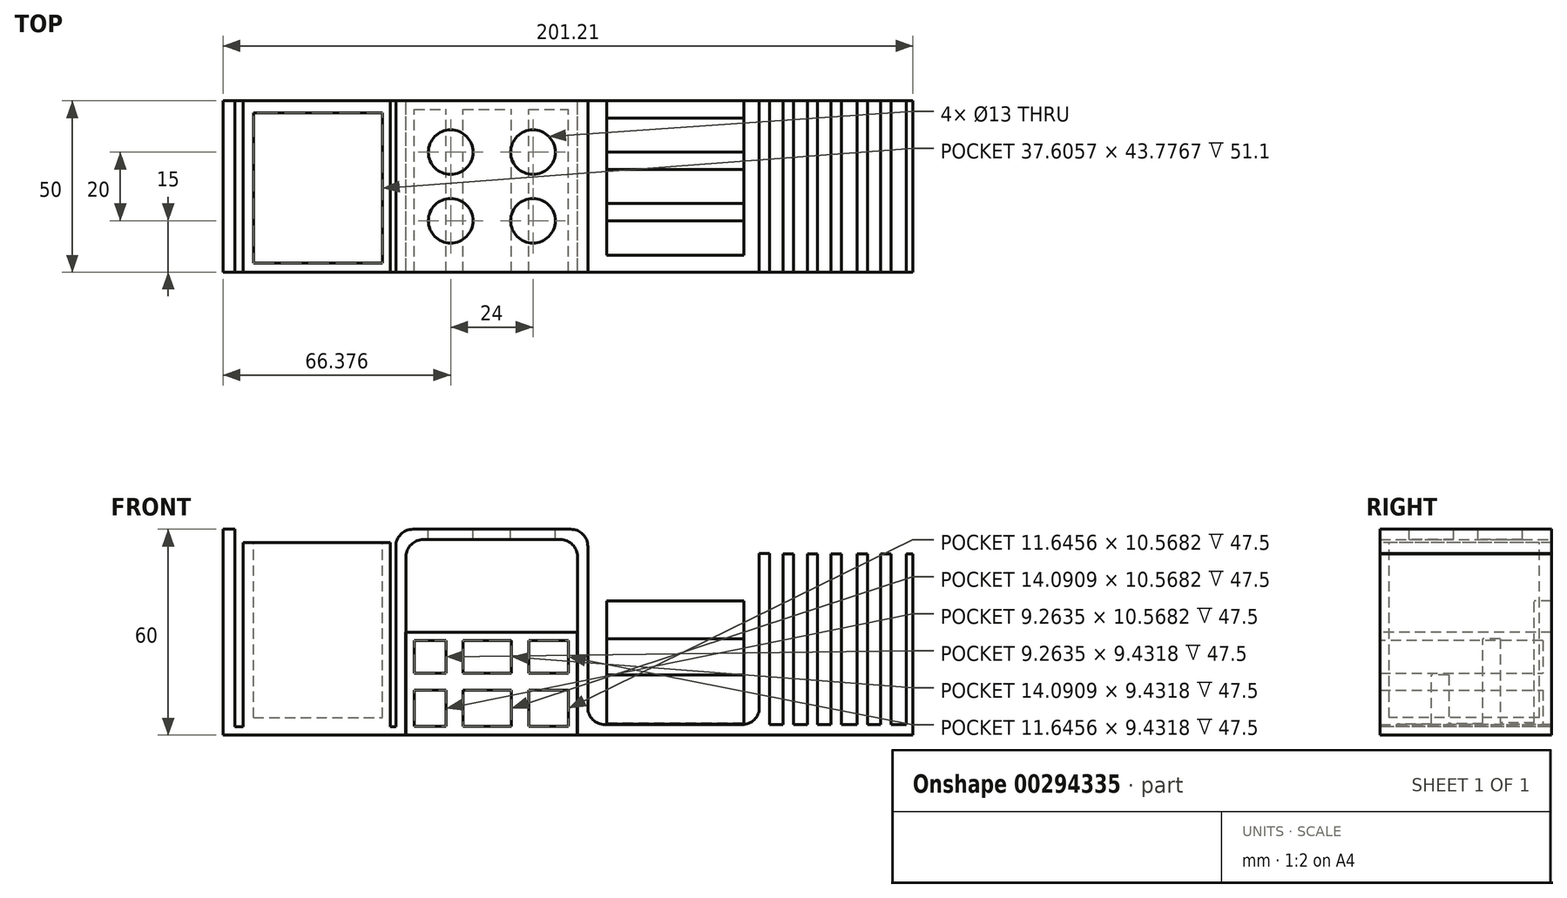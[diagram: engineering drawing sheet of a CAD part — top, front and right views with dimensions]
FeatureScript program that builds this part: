
annotation { "Feature Type Name" : "Feature", "Feature Type Description" : "" }
export const myFeature = defineFeature(function(context is Context, id is Id, definition is map)
    precondition{}
    {
        {
            var Q0;
            Q0=qCreatedBy(makeId("Front.planeOp"),FACE);
            var sketch = newSketch(context, id + "F0", { "sketchPlane" : qUnion([Q0])});
            skLineSegment(sketch, "E0.top", {"start": v(4.58, 57) * mm, "end": v(54.58, 57) * mm});
            skLineSegment(sketch, "E0.left", {"start": v(4.58, 0) * mm, "end": v(4.58, 57) * mm});
            skLineSegment(sketch, "E0.right", {"start": v(54.58, 0) * mm, "end": v(54.58, 57) * mm});
            skLineSegment(sketch, "E1.top", {"start": v(57.58, 3) * mm, "end": v(107.58, 3) * mm});
            skLineSegment(sketch, "E1.left", {"start": v(57.58, 60) * mm, "end": v(57.58, 3) * mm});
            skLineSegment(sketch, "E1.right", {"start": v(107.58, 53) * mm, "end": v(107.58, 3) * mm});
            skLineSegment(sketch, "E2", {"start": v(1.58, 0) * mm, "end": v(4.58, 0) * mm});
            skLineSegment(sketch, "E3", {"start": v(54.58, 0) * mm, "end": v(110.58, 0) * mm});
            skLineSegment(sketch, "E4", {"start": v(1.58, 60) * mm, "end": v(57.58, 60) * mm});
            skLineSegment(sketch, "E5", {"start": v(110.58, 53) * mm, "end": v(107.58, 53) * mm});
            skLineSegment(sketch, "E6.bottom", {"start": v(1.58, 0) * mm, "end": v(-45.36, 0) * mm});
            skLineSegment(sketch, "E6.top", {"start": v(1.58, 2.45) * mm, "end": v(-45.36, 2.45) * mm});
            skLineSegment(sketch, "E7.bottom", {"start": v(-45.36, 0) * mm, "end": v(-48.8, 0) * mm});
            skLineSegment(sketch, "E7.top", {"start": v(-45.36, 60) * mm, "end": v(-48.8, 60) * mm});
            skLineSegment(sketch, "E7.right", {"start": v(-48.8, 0) * mm, "end": v(-48.8, 60) * mm});
            skLineSegment(sketch, "E8", {"start": v(-45.36, 60) * mm, "end": v(-45.36, 2.45) * mm});
            skLineSegment(sketch, "E9", {"start": v(1.58, 60) * mm, "end": v(1.58, 2.45) * mm});
            skLineSegment(sketch, "E10.bottom", {"start": v(110.58, 0) * mm, "end": v(152.41, 0) * mm});
            skLineSegment(sketch, "E10.top", {"start": v(110.58, 3.01) * mm, "end": v(152.41, 3.01) * mm});
            skLineSegment(sketch, "E10.right", {"start": v(152.41, 0) * mm, "end": v(152.41, 3.01) * mm});
            skLineSegment(sketch, "E11", {"start": v(110.58, 53) * mm, "end": v(110.58, 3.01) * mm});
            skLineSegment(sketch, "E12.bottom", {"start": v(114.5, 3.01) * mm, "end": v(117.5, 3.01) * mm});
            skLineSegment(sketch, "E12.top", {"start": v(114.5, 52.83) * mm, "end": v(117.5, 52.83) * mm});
            skLineSegment(sketch, "E12.left", {"start": v(114.5, 3.01) * mm, "end": v(114.5, 52.83) * mm});
            skLineSegment(sketch, "E12.right", {"start": v(117.5, 3.01) * mm, "end": v(117.5, 52.83) * mm});
            skLineSegment(sketch, "E13.bottom", {"start": v(121.6, 3.01) * mm, "end": v(124.6, 3.01) * mm});
            skLineSegment(sketch, "E13.top", {"start": v(121.6, 52.83) * mm, "end": v(124.6, 52.83) * mm});
            skLineSegment(sketch, "E13.left", {"start": v(121.6, 3.01) * mm, "end": v(121.6, 52.83) * mm});
            skLineSegment(sketch, "E13.right", {"start": v(124.6, 3.01) * mm, "end": v(124.6, 52.83) * mm});
            skLineSegment(sketch, "E14.bottom", {"start": v(128.48, 3.01) * mm, "end": v(131.48, 3.01) * mm});
            skLineSegment(sketch, "E14.top", {"start": v(128.48, 52.83) * mm, "end": v(131.48, 52.83) * mm});
            skLineSegment(sketch, "E14.left", {"start": v(128.48, 3.01) * mm, "end": v(128.48, 52.83) * mm});
            skLineSegment(sketch, "E14.right", {"start": v(131.48, 3.01) * mm, "end": v(131.48, 52.83) * mm});
            skLineSegment(sketch, "E15.bottom", {"start": v(136.1, 3.01) * mm, "end": v(139.1, 3.01) * mm});
            skLineSegment(sketch, "E15.top", {"start": v(136.1, 52.83) * mm, "end": v(139.1, 52.83) * mm});
            skLineSegment(sketch, "E15.left", {"start": v(136.1, 3.01) * mm, "end": v(136.1, 52.83) * mm});
            skLineSegment(sketch, "E15.right", {"start": v(139.1, 3.01) * mm, "end": v(139.1, 52.83) * mm});
            skLineSegment(sketch, "E16.bottom", {"start": v(142.98, 3.01) * mm, "end": v(145.98, 3.01) * mm});
            skLineSegment(sketch, "E16.top", {"start": v(142.98, 52.83) * mm, "end": v(145.98, 52.83) * mm});
            skLineSegment(sketch, "E16.left", {"start": v(142.98, 3.01) * mm, "end": v(142.98, 52.83) * mm});
            skLineSegment(sketch, "E16.right", {"start": v(145.98, 3.01) * mm, "end": v(145.98, 52.83) * mm});
            skLineSegment(sketch, "E17.bottom", {"start": v(152.41, 3.01) * mm, "end": v(150.41, 3.01) * mm});
            skLineSegment(sketch, "E17.top", {"start": v(152.41, 52.83) * mm, "end": v(150.41, 52.83) * mm});
            skLineSegment(sketch, "E17.left", {"start": v(152.41, 3.01) * mm, "end": v(152.41, 52.83) * mm});
            skLineSegment(sketch, "E17.right", {"start": v(150.41, 3.01) * mm, "end": v(150.41, 52.83) * mm});
            skLineSegment(sketch, "E18", {"start": v(107.58, 3) * mm, "end": v(107.58, 0) * mm});
            skSolve(sketch);
        }
        {
            var Q0;
            Q0 = qSketchRegion(id + "F0", true);
            extrude(context, id + "F1", {"entities" : qUnion([Q0]), "depth" : 50 * mm, "offsetDistance" : 25 * mm});
        }
        {
            var Q0;
            Q0=makeQuery(id+"F1.opExtrude","SWEPT_FACE",FACE,{"disambiguationData":[OSD([sQuery(id+"F0.wireOp",EDGE,"E4")])]});
            var sketch = newSketch(context, id + "F2", { "sketchPlane" : qUnion([Q0])});
            skCircle(sketch, "E19", {"center": v(17.58, -15) * mm, "radius": 6.5 * mm});
            skCircle(sketch, "E20", {"center": v(41.58, -15) * mm, "radius": 6.5 * mm});
            skCircle(sketch, "E21", {"center": v(17.58, -35) * mm, "radius": 6.5 * mm});
            skCircle(sketch, "E22", {"center": v(41.58, -35) * mm, "radius": 6.5 * mm});
            skSolve(sketch);
        }
        {
            var Q0;
            Q0=qCreatedBy(makeId("Top.planeOp"),FACE);
            var sketch = newSketch(context, id + "F3", { "sketchPlane" : qUnion([Q0])});
            skLineSegment(sketch, "E23.bottom", {"start": v(4.44, 0) * mm, "end": v(54.44, 0) * mm});
            skLineSegment(sketch, "E23.top", {"start": v(4.44, -50) * mm, "end": v(54.44, -50) * mm});
            skLineSegment(sketch, "E23.left", {"start": v(4.44, 0) * mm, "end": v(4.44, -50) * mm});
            skLineSegment(sketch, "E23.right", {"start": v(54.44, 0) * mm, "end": v(54.44, -50) * mm});
            skSolve(sketch);
        }
        {
            var Q0;
            Q0=makeQuery(id+"F1.opExtrude","SWEPT_FACE",FACE,{"disambiguationData":[OSD([sQuery(id+"F0.wireOp",EDGE,"E1.top")])]});
            var sketch = newSketch(context, id + "F4", { "sketchPlane" : qUnion([Q0])});
            skLineSegment(sketch, "E24.bottom", {"start": v(63.1, 0) * mm, "end": v(103.1, 0) * mm});
            skLineSegment(sketch, "E24.top", {"start": v(63.1, -15) * mm, "end": v(103.1, -15) * mm});
            skLineSegment(sketch, "E24.left", {"start": v(63.1, 0) * mm, "end": v(63.1, -15) * mm});
            skLineSegment(sketch, "E24.right", {"start": v(103.1, 0) * mm, "end": v(103.1, -15) * mm});
            skSolve(sketch);
        }
        {
            var Q0;
            Q0 = qSketchRegion(id + "F4", true);
            extrude(context, id + "F5", {"entities" : qUnion([Q0]), "operationType" : NewBodyOperationType.ADD, "depth" : 36.1 * mm});
        }
        {
            var Q0;
            Q0=makeQuery(id+"F5.opExtrude","CAP_FACE",FACE,{"disambiguationData":[OSD([sQuery(id+"F4.wireOp",EDGE,"E24.bottom"),sQuery(id+"F4.wireOp",EDGE,"E24.top"),sQuery(id+"F4.wireOp",EDGE,"E24.left"),sQuery(id+"F4.wireOp",EDGE,"E24.right")])],"isStart":false});
            var sketch = newSketch(context, id + "F6", { "sketchPlane" : qUnion([Q0])});
            skLineSegment(sketch, "E25.bottom", {"start": v(63.1, -15) * mm, "end": v(103.1, -15) * mm});
            skLineSegment(sketch, "E25.top", {"start": v(63.1, -5) * mm, "end": v(103.1, -5) * mm});
            skLineSegment(sketch, "E25.left", {"start": v(63.1, -15) * mm, "end": v(63.1, -5) * mm});
            skLineSegment(sketch, "E25.right", {"start": v(103.1, -15) * mm, "end": v(103.1, -5) * mm});
            skSolve(sketch);
        }
        {
            var Q0;
            Q0 = qSketchRegion(id + "F6", true);
            extrude(context, id + "F7", {"entities" : qUnion([Q0]), "operationType" : NewBodyOperationType.REMOVE, "oppositeDirection" : true, "depth" : 35.5 * mm});
        }
        {
            var Q0;
            Q0=makeQuery(id+"F1.opExtrude","SWEPT_FACE",FACE,{"disambiguationData":[OSD([sQuery(id+"F0.wireOp",EDGE,"E1.top")])]});
            var sketch = newSketch(context, id + "F8", { "sketchPlane" : qUnion([Q0])});
            skLineSegment(sketch, "E26.bottom", {"start": v(63.1, -15) * mm, "end": v(103.1, -15) * mm});
            skLineSegment(sketch, "E26.top", {"start": v(63.1, -30) * mm, "end": v(103.1, -30) * mm});
            skLineSegment(sketch, "E26.left", {"start": v(63.1, -15) * mm, "end": v(63.1, -30) * mm});
            skLineSegment(sketch, "E26.right", {"start": v(103.1, -15) * mm, "end": v(103.1, -30) * mm});
            skSolve(sketch);
        }
        {
            var Q0;
            Q0 = qSketchRegion(id + "F8", true);
            extrude(context, id + "F9", {"entities" : qUnion([Q0]), "operationType" : NewBodyOperationType.ADD, "depth" : 25.1 * mm});
        }
        {
            var Q0;
            Q0=makeQuery(id+"F9.opExtrude","CAP_FACE",FACE,{"disambiguationData":[OSD([sQuery(id+"F8.wireOp",EDGE,"E26.bottom"),sQuery(id+"F8.wireOp",EDGE,"E26.top"),sQuery(id+"F8.wireOp",EDGE,"E26.left"),sQuery(id+"F8.wireOp",EDGE,"E26.right")])],"isStart":false});
            var sketch = newSketch(context, id + "F10", { "sketchPlane" : qUnion([Q0])});
            skLineSegment(sketch, "E27.bottom", {"start": v(63.1, -30) * mm, "end": v(103.1, -30) * mm});
            skLineSegment(sketch, "E27.top", {"start": v(63.1, -20) * mm, "end": v(103.1, -20) * mm});
            skLineSegment(sketch, "E27.left", {"start": v(63.1, -30) * mm, "end": v(63.1, -20) * mm});
            skLineSegment(sketch, "E27.right", {"start": v(103.1, -30) * mm, "end": v(103.1, -20) * mm});
            skSolve(sketch);
        }
        {
            var Q0;
            Q0 = qSketchRegion(id + "F10", true);
            extrude(context, id + "F11", {"entities" : qUnion([Q0]), "operationType" : NewBodyOperationType.REMOVE, "oppositeDirection" : true, "depth" : 24.8 * mm});
        }
        {
            var Q0;
            Q0=makeQuery(id+"F1.opExtrude","SWEPT_FACE",FACE,{"disambiguationData":[OSD([sQuery(id+"F0.wireOp",EDGE,"E1.top")])]});
            var sketch = newSketch(context, id + "F12", { "sketchPlane" : qUnion([Q0])});
            skLineSegment(sketch, "E28.bottom", {"start": v(63.1, -30) * mm, "end": v(103.1, -30) * mm});
            skLineSegment(sketch, "E28.top", {"start": v(63.1, -45) * mm, "end": v(103.1, -45) * mm});
            skLineSegment(sketch, "E28.left", {"start": v(63.1, -30) * mm, "end": v(63.1, -45) * mm});
            skLineSegment(sketch, "E28.right", {"start": v(103.1, -30) * mm, "end": v(103.1, -45) * mm});
            skSolve(sketch);
        }
        {
            var Q0;
            Q0 = qSketchRegion(id + "F12", true);
            extrude(context, id + "F13", {"entities" : qUnion([Q0]), "operationType" : NewBodyOperationType.ADD, "depth" : 14.5 * mm});
        }
        {
            var Q0;
            Q0=makeQuery(id+"F13.opExtrude","CAP_FACE",FACE,{"disambiguationData":[OSD([sQuery(id+"F12.wireOp",EDGE,"E28.bottom"),sQuery(id+"F12.wireOp",EDGE,"E28.top"),sQuery(id+"F12.wireOp",EDGE,"E28.left"),sQuery(id+"F12.wireOp",EDGE,"E28.right")])],"isStart":false});
            var sketch = newSketch(context, id + "F14", { "sketchPlane" : qUnion([Q0])});
            skLineSegment(sketch, "E29.bottom", {"start": v(63.1, -45) * mm, "end": v(103.1, -45) * mm});
            skLineSegment(sketch, "E29.top", {"start": v(63.1, -35) * mm, "end": v(103.1, -35) * mm});
            skLineSegment(sketch, "E29.left", {"start": v(63.1, -45) * mm, "end": v(63.1, -35) * mm});
            skLineSegment(sketch, "E29.right", {"start": v(103.1, -45) * mm, "end": v(103.1, -35) * mm});
            skSolve(sketch);
        }
        {
            var Q0;
            Q0 = qSketchRegion(id + "F14", true);
            extrude(context, id + "F15", {"entities" : qUnion([Q0]), "operationType" : NewBodyOperationType.REMOVE, "oppositeDirection" : true, "depth" : 14.3 * mm});
        }
        {
            var Q0;
            Q0=makeQuery(id+"F1.opExtrude","SWEPT_EDGE",EDGE,{"disambiguationData":[OSD([sQuery(id+"F0.wireOp",EDGE,"E1.left"),sQuery(id+"F0.wireOp",EDGE,"E4")])]});
            var Q1;
            Q1=makeQuery(id+"F1.opExtrude","SWEPT_EDGE",EDGE,{"disambiguationData":[OSD([sQuery(id+"F0.wireOp",EDGE,"E0.top"),sQuery(id+"F0.wireOp",EDGE,"E0.right")])]});
            var Q2;
            Q2=makeQuery(id+"F1.opExtrude","SWEPT_EDGE",EDGE,{"disambiguationData":[OSD([sQuery(id+"F0.wireOp",EDGE,"xXto4Pc0-SdtI-9WrI-qXPa-qfZvLXBMMGb8.left"),sQuery(id+"F0.wireOp",EDGE,"E4")])]});
            var Q3;
            Q3=makeQuery(id+"F1.opExtrude","SWEPT_EDGE",EDGE,{"disambiguationData":[OSD([sQuery(id+"F0.wireOp",EDGE,"E0.top"),sQuery(id+"F0.wireOp",EDGE,"E0.left")])]});
            var Q4;
            Q4=makeQuery(id+"F1.opExtrude","SWEPT_EDGE",EDGE,{"disambiguationData":[OSD([sQuery(id+"F0.wireOp",EDGE,"E1.top"),sQuery(id+"F0.wireOp",EDGE,"E1.left")])]});
            var Q5;
            Q5=makeQuery(id+"F1.opExtrude","SWEPT_EDGE",EDGE,{"disambiguationData":[OSD([sQuery(id+"F0.wireOp",EDGE,"E1.top"),sQuery(id+"F0.wireOp",EDGE,"E1.right")])]});
            fillet(context, id + "F16", {"entities" : qUnion([Q0, Q1, Q2, Q3, Q4, Q5]), "radius" : 5 * mm, "tangentPropagation" : true, "allowEdgeOverflow" : false});
        }
        {
            var Q0;
            Q0 = qSketchRegion(id + "F3", true);
            extrude(context, id + "F17", {"entities" : qUnion([Q0]), "depth" : 30 * mm});
        }
        {
            var Q0;
            Q0=makeQuery(id+"F17.opExtrude","SWEPT_FACE",FACE,{"disambiguationData":[OSD([sQuery(id+"F3.wireOp",EDGE,"E23.top")])]});
            shell(context, id + "F18", {"entities" : qUnion([Q0]), "thickness" : 2.5 * mm});
        }
        {
            var Q0;
            Q0 = qSketchRegion(id + "F2", true);
            var Q1;
            Q1 = qSketchRegion(id + "F10", true);
            extrude(context, id + "F19", {"entities" : qUnion([Q0, Q1]), "operationType" : NewBodyOperationType.REMOVE, "oppositeDirection" : true, "depth" : 13.9 * mm});
        }
        {
            var Q0;
            Q0=makeQuery(id+"F1.opExtrude","SWEPT_FACE",FACE,{"disambiguationData":[OSD([sQuery(id+"F0.wireOp",EDGE,"E6.top")])]});
            var sketch = newSketch(context, id + "F20", { "sketchPlane" : qUnion([Q0])});
            skLineSegment(sketch, "E30.bottom", {"start": v(-43, 0) * mm, "end": v(0, 0) * mm});
            skLineSegment(sketch, "E30.top", {"start": v(-43, -50) * mm, "end": v(0, -50) * mm});
            skLineSegment(sketch, "E30.left", {"start": v(-43, 0) * mm, "end": v(-43, -50) * mm});
            skLineSegment(sketch, "E30.right", {"start": v(0, 0) * mm, "end": v(0, -50) * mm});
            skSolve(sketch);
        }
        {
            var Q0;
            Q0 = qSketchRegion(id + "F20", true);
            extrude(context, id + "F21", {"entities" : qUnion([Q0]), "operationType" : NewBodyOperationType.ADD, "depth" : 53.7 * mm});
        }
        {
            var Q0;
            Q0=makeQuery(id+"F21.opExtrude","CAP_FACE",FACE,{"disambiguationData":[OSD([sQuery(id+"F20.wireOp",EDGE,"E30.bottom"),sQuery(id+"F20.wireOp",EDGE,"E30.top"),sQuery(id+"F20.wireOp",EDGE,"E30.left"),sQuery(id+"F20.wireOp",EDGE,"E30.right")])],"isStart":false});
            var sketch = newSketch(context, id + "F22", { "sketchPlane" : qUnion([Q0])});
            skLineSegment(sketch, "E31.bottom", {"start": v(-39.95, -3.55) * mm, "end": v(-2.35, -3.55) * mm});
            skLineSegment(sketch, "E31.top", {"start": v(-39.95, -47.33) * mm, "end": v(-2.35, -47.33) * mm});
            skLineSegment(sketch, "E31.left", {"start": v(-39.95, -3.55) * mm, "end": v(-39.95, -47.33) * mm});
            skLineSegment(sketch, "E31.right", {"start": v(-2.35, -3.55) * mm, "end": v(-2.35, -47.33) * mm});
            skSolve(sketch);
        }
        {
            var Q0;
            Q0 = qSketchRegion(id + "F22", true);
            extrude(context, id + "F23", {"entities" : qUnion([Q0]), "operationType" : NewBodyOperationType.REMOVE, "oppositeDirection" : true, "depth" : 51.1 * mm});
        }
        {
            var Q0;
            Q0=makeQuery(id+"F18.opShell","OFFSET_FACE",FACE,{"disambiguationData":[OSD([sQuery(id+"F3.wireOp",EDGE,"E23.bottom")])]});
            var sketch = newSketch(context, id + "F24", { "sketchPlane" : qUnion([Q0])});
            skLineSegment(sketch, "E32.bottom", {"start": v(6.94, 18.07) * mm, "end": v(51.94, 18.07) * mm});
            skLineSegment(sketch, "E32.top", {"start": v(6.94, 13.07) * mm, "end": v(51.94, 13.07) * mm});
            skLineSegment(sketch, "E32.left", {"start": v(6.94, 18.07) * mm, "end": v(6.94, 13.07) * mm});
            skLineSegment(sketch, "E32.right", {"start": v(51.94, 18.07) * mm, "end": v(51.94, 13.07) * mm});
            skLineSegment(sketch, "E33.bottom", {"start": v(16.2, 27.5) * mm, "end": v(21.2, 27.5) * mm});
            skLineSegment(sketch, "E33.top", {"start": v(16.2, 2.5) * mm, "end": v(21.2, 2.5) * mm});
            skLineSegment(sketch, "E33.left", {"start": v(16.2, 27.5) * mm, "end": v(16.2, 2.5) * mm});
            skLineSegment(sketch, "E33.right", {"start": v(21.2, 27.5) * mm, "end": v(21.2, 2.5) * mm});
            skLineSegment(sketch, "E34.bottom", {"start": v(35.3, 27.5) * mm, "end": v(40.3, 27.5) * mm});
            skLineSegment(sketch, "E34.top", {"start": v(35.3, 2.5) * mm, "end": v(40.3, 2.5) * mm});
            skLineSegment(sketch, "E34.left", {"start": v(35.3, 27.5) * mm, "end": v(35.3, 2.5) * mm});
            skLineSegment(sketch, "E34.right", {"start": v(40.3, 27.5) * mm, "end": v(40.3, 2.5) * mm});
            skSolve(sketch);
        }
        {
            var Q0;
            Q0 = qSketchRegion(id + "F24", true);
            extrude(context, id + "F25", {"entities" : qUnion([Q0]), "operationType" : NewBodyOperationType.ADD, "depth" : 47.5 * mm});
        }
    });
